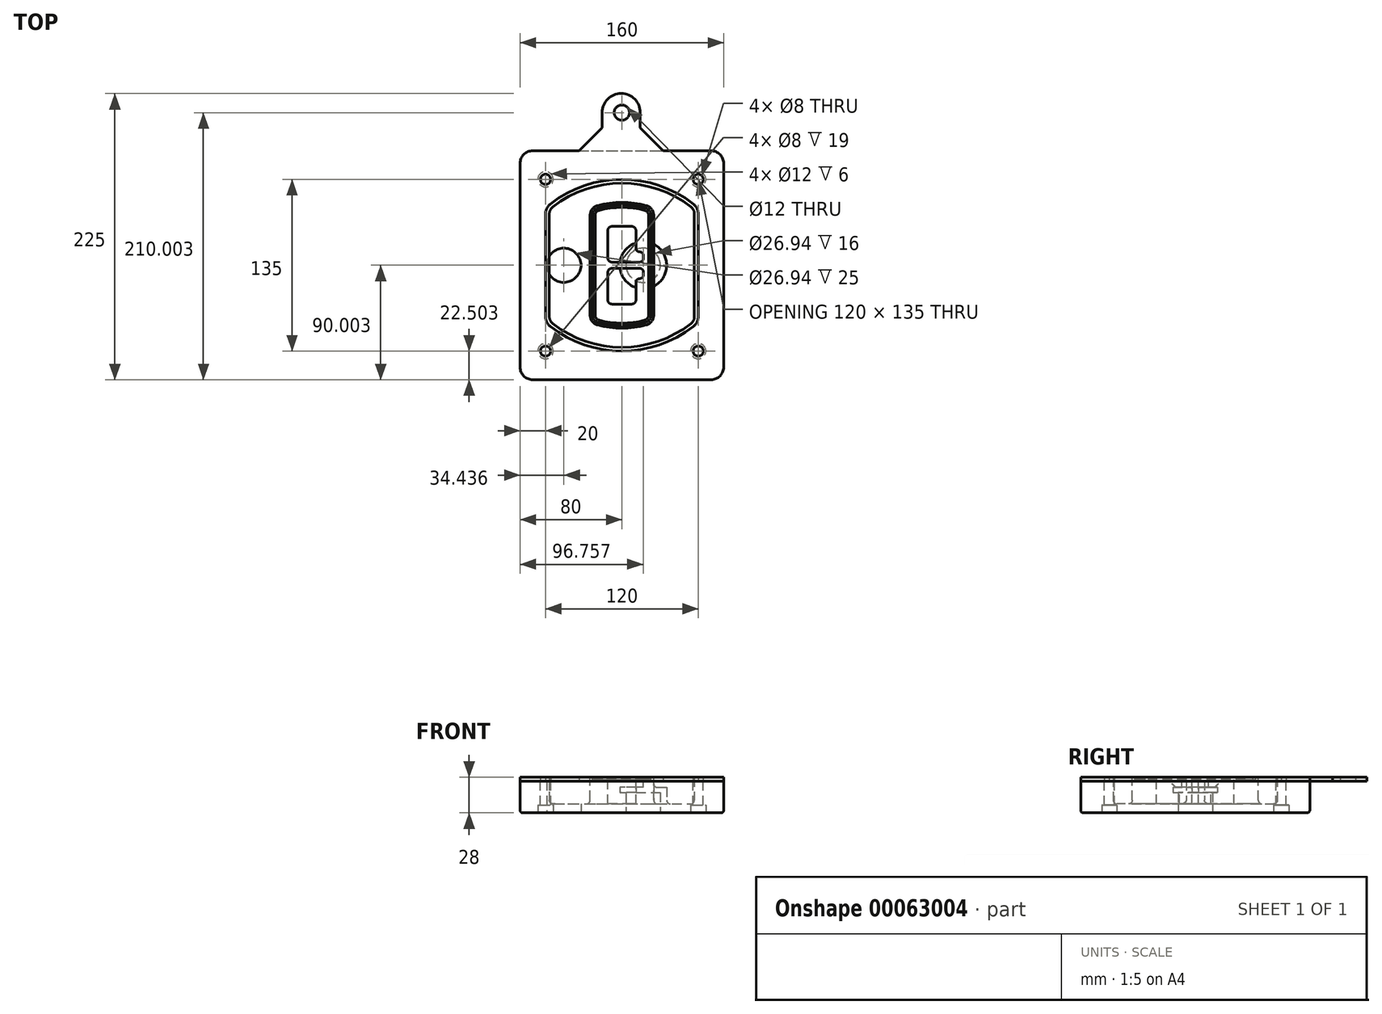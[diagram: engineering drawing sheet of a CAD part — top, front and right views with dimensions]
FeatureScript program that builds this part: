
annotation { "Feature Type Name" : "Feature", "Feature Type Description" : "" }
export const myFeature = defineFeature(function(context is Context, id is Id, definition is map)
    precondition{}
    {
        {
            var Q0;
            Q0=qCreatedBy(makeId("Top.planeOp"),FACE);
            var sketch = newSketch(context, id + "F0", { "sketchPlane" : qUnion([Q0])});
            skPoint(sketch, "E0.rect.middle", {"position": v(0, 0) * mm});
            skLineSegment(sketch, "E1.bottom", {"start": v(24.05, 28.38) * mm, "end": v(164.05, 28.38) * mm});
            skLineSegment(sketch, "E1.top", {"start": v(24.05, 208.38) * mm, "end": v(164.05, 208.38) * mm});
            skLineSegment(sketch, "E1.left", {"start": v(14.05, 38.38) * mm, "end": v(14.05, 198.38) * mm});
            skLineSegment(sketch, "E1.right", {"start": v(174.05, 38.38) * mm, "end": v(174.05, 198.38) * mm});
            skLineSegment(sketch, "E2", {"start": v(14.05, 208.38) * mm, "end": v(174.05, 28.38) * mm, "construction": true});
            skLineSegment(sketch, "E3", {"start": v(174.05, 208.38) * mm, "end": v(14.05, 28.38) * mm, "construction": true});
            skCircle(sketch, "E4", {"center": v(34.05, 185.88) * mm, "radius": 4 * mm});
            skCircle(sketch, "E5", {"center": v(154.05, 185.88) * mm, "radius": 4 * mm});
            skCircle(sketch, "E6", {"center": v(154.05, 50.88) * mm, "radius": 4 * mm});
            skCircle(sketch, "E7", {"center": v(34.05, 50.88) * mm, "radius": 4 * mm});
            skLineSegment(sketch, "E8", {"start": v(34.05, 185.88) * mm, "end": v(154.05, 185.88) * mm, "construction": true});
            skLineSegment(sketch, "E9", {"start": v(154.05, 185.88) * mm, "end": v(154.05, 50.88) * mm, "construction": true});
            skLineSegment(sketch, "E10", {"start": v(154.05, 50.88) * mm, "end": v(34.05, 50.88) * mm, "construction": true});
            skLineSegment(sketch, "E11", {"start": v(34.05, 50.88) * mm, "end": v(34.05, 185.88) * mm, "construction": true});
            skLineSegment(sketch, "E12", {"start": v(34.05, 158.68) * mm, "end": v(34.05, 78.09) * mm});
            skLineSegment(sketch, "E13", {"start": v(154.05, 158.68) * mm, "end": v(154.05, 78.09) * mm});
            skArc(sketch, "E14", {"start": v(150.2, 166.56) * mm, "mid": v(94.05, 185.88) * mm, "end": v(37.9, 166.56) * mm});
            skArc(sketch, "E15", {"start": v(37.9, 70.2) * mm, "mid": v(94.05, 50.88) * mm, "end": v(150.2, 70.2) * mm});
            skLineSegment(sketch, "E16", {"start": v(34.05, 118.38) * mm, "end": v(154.05, 118.38) * mm, "construction": true});
            skPoint(sketch, "E17.visualSharp", {"position": v(34.05, 73.38) * mm});
            skArc(sketch, "E17.filletArc", {"start": v(34.05, 78.09) * mm, "mid": v(35.06, 73.7) * mm, "end": v(37.9, 70.2) * mm});
            skPoint(sketch, "E18.visualSharp", {"position": v(34.05, 163.38) * mm});
            skArc(sketch, "E18.filletArc", {"start": v(37.9, 166.56) * mm, "mid": v(35.06, 163.06) * mm, "end": v(34.05, 158.68) * mm});
            skPoint(sketch, "E19.visualSharp", {"position": v(154.05, 163.38) * mm});
            skArc(sketch, "E19.filletArc", {"start": v(154.05, 158.68) * mm, "mid": v(153.04, 163.06) * mm, "end": v(150.2, 166.56) * mm});
            skPoint(sketch, "E20.visualSharp", {"position": v(154.05, 73.38) * mm});
            skArc(sketch, "E20.filletArc", {"start": v(150.2, 70.2) * mm, "mid": v(153.04, 73.7) * mm, "end": v(154.05, 78.09) * mm});
            skPoint(sketch, "E21.visualSharp", {"position": v(14.05, 208.38) * mm});
            skArc(sketch, "E21.filletArc", {"start": v(24.05, 208.38) * mm, "mid": v(16.98, 205.45) * mm, "end": v(14.05, 198.38) * mm});
            skPoint(sketch, "E22.visualSharp", {"position": v(174.05, 208.38) * mm});
            skArc(sketch, "E22.filletArc", {"start": v(174.05, 198.38) * mm, "mid": v(171.12, 205.45) * mm, "end": v(164.05, 208.38) * mm});
            skPoint(sketch, "E23.visualSharp", {"position": v(174.05, 28.38) * mm});
            skArc(sketch, "E23.filletArc", {"start": v(164.05, 28.38) * mm, "mid": v(171.12, 31.31) * mm, "end": v(174.05, 38.38) * mm});
            skPoint(sketch, "E24.visualSharp", {"position": v(14.05, 28.38) * mm});
            skArc(sketch, "E24.filletArc", {"start": v(14.05, 38.38) * mm, "mid": v(16.98, 31.31) * mm, "end": v(24.05, 28.38) * mm});
            skArc(sketch, "E25.0", {"start": v(151.05, 158.68) * mm, "mid": v(150.34, 161.75) * mm, "end": v(148.36, 164.2) * mm});
            skLineSegment(sketch, "E25.1", {"start": v(151.05, 158.68) * mm, "end": v(151.05, 78.09) * mm});
            skArc(sketch, "E25.2", {"start": v(148.36, 72.57) * mm, "mid": v(150.34, 75.02) * mm, "end": v(151.05, 78.09) * mm});
            skArc(sketch, "E25.3", {"start": v(39.74, 72.57) * mm, "mid": v(94.05, 53.88) * mm, "end": v(148.36, 72.57) * mm});
            skArc(sketch, "E25.4", {"start": v(37.05, 78.09) * mm, "mid": v(37.76, 75.02) * mm, "end": v(39.74, 72.57) * mm});
            skArc(sketch, "E25.5", {"start": v(148.36, 164.2) * mm, "mid": v(94.05, 182.88) * mm, "end": v(39.74, 164.2) * mm});
            skLineSegment(sketch, "E25.6", {"start": v(37.05, 158.68) * mm, "end": v(37.05, 78.09) * mm});
            skArc(sketch, "E25.7", {"start": v(39.74, 164.2) * mm, "mid": v(37.76, 161.75) * mm, "end": v(37.05, 158.68) * mm});
            skArc(sketch, "E26.0", {"start": v(35.43, 169.71) * mm, "mid": v(31.47, 164.82) * mm, "end": v(30.05, 158.68) * mm});
            skArc(sketch, "E26.1", {"start": v(152.67, 169.71) * mm, "mid": v(94.05, 189.88) * mm, "end": v(35.43, 169.71) * mm});
            skArc(sketch, "E26.2", {"start": v(158.05, 158.68) * mm, "mid": v(156.63, 164.82) * mm, "end": v(152.67, 169.71) * mm});
            skLineSegment(sketch, "E26.3", {"start": v(158.05, 158.68) * mm, "end": v(158.05, 78.09) * mm});
            skArc(sketch, "E26.4", {"start": v(152.67, 67.05) * mm, "mid": v(156.63, 71.95) * mm, "end": v(158.05, 78.09) * mm});
            skLineSegment(sketch, "E26.5", {"start": v(30.05, 158.68) * mm, "end": v(30.05, 78.09) * mm});
            skArc(sketch, "E26.6", {"start": v(35.43, 67.05) * mm, "mid": v(94.05, 46.88) * mm, "end": v(152.67, 67.05) * mm});
            skArc(sketch, "E26.7", {"start": v(30.05, 78.09) * mm, "mid": v(31.47, 71.95) * mm, "end": v(35.43, 67.05) * mm});
            skSolve(sketch);
        }
        {
            var Q0;
            Q0=makeQuery(id+"F0.imprint","IMPRINT",FACE,{"disambiguationData":[TD([[makeQuery(id+"F0.imprint","IMPRINT",EDGE,{"derivedFrom":sQuery(id+"F0.wireOp",EDGE,"E1.bottom")}),1.0]])]});
            var Q1;
            Q1=makeQuery(id+"F0.imprint","IMPRINT",FACE,{"disambiguationData":[TD([[makeQuery(id+"F0.imprint","IMPRINT",EDGE,{"derivedFrom":sQuery(id+"F0.wireOp",EDGE,"E12")}),1.0]])]});
            var Q2;
            Q2=makeQuery(id+"F0.imprint","IMPRINT",FACE,{"disambiguationData":[TD([[makeQuery(id+"F0.imprint","IMPRINT",EDGE,{"derivedFrom":sQuery(id+"F0.wireOp",EDGE,"E25.0")}),1.0]])]});
            var Q3;
            Q3=makeQuery(id+"F0.imprint","IMPRINT",FACE,{"disambiguationData":[TD([[makeQuery(id+"F0.imprint","IMPRINT",EDGE,{"derivedFrom":sQuery(id+"F0.wireOp",EDGE,"E12")}),-1.0]])]});
            extrude(context, id + "F1", {"entities" : qUnion([Q0, Q1, Q2, Q3]), "oppositeDirection" : true, "depth" : 25 * mm});
        }
        {
            var Q0;
            Q0=makeQuery(id+"F0.imprint","IMPRINT",FACE,{"disambiguationData":[TD([[makeQuery(id+"F0.imprint","IMPRINT",EDGE,{"derivedFrom":sQuery(id+"F0.wireOp",EDGE,"E12")}),1.0]])]});
            extrude(context, id + "F2", {"entities" : qUnion([Q0]), "operationType" : NewBodyOperationType.ADD, "depth" : 3 * mm});
        }
        {
            var Q0;
            Q0=makeQuery(id+"F0.imprint","IMPRINT",FACE,{"disambiguationData":[TD([[makeQuery(id+"F0.imprint","IMPRINT",EDGE,{"derivedFrom":sQuery(id+"F0.wireOp",EDGE,"E25.0")}),1.0]])]});
            extrude(context, id + "F3", {"entities" : qUnion([Q0]), "operationType" : NewBodyOperationType.REMOVE, "oppositeDirection" : true, "depth" : 18 * mm});
        }
        {
            var Q0;
            Q0=makeQuery(id+"F2.opExtrude","CAP_FACE",FACE,{"disambiguationData":[OSD([sQuery(id+"F0.wireOp",EDGE,"E12"),sQuery(id+"F0.wireOp",EDGE,"E13"),sQuery(id+"F0.wireOp",EDGE,"E14"),sQuery(id+"F0.wireOp",EDGE,"E15"),sQuery(id+"F0.wireOp",EDGE,"E17.filletArc"),sQuery(id+"F0.wireOp",EDGE,"E18.filletArc"),sQuery(id+"F0.wireOp",EDGE,"E19.filletArc"),sQuery(id+"F0.wireOp",EDGE,"E20.filletArc"),sQuery(id+"F0.wireOp",EDGE,"E25.0"),sQuery(id+"F0.wireOp",EDGE,"E25.1"),sQuery(id+"F0.wireOp",EDGE,"E25.2"),sQuery(id+"F0.wireOp",EDGE,"E25.3"),sQuery(id+"F0.wireOp",EDGE,"E25.4"),sQuery(id+"F0.wireOp",EDGE,"E25.5"),sQuery(id+"F0.wireOp",EDGE,"E25.6"),sQuery(id+"F0.wireOp",EDGE,"E25.7")])],"isStart":false});
            var sketch = newSketch(context, id + "F4", { "sketchPlane" : qUnion([Q0])});
            skArc(sketch, "E27.0", {"start": v(74.97, 71.41) * mm, "mid": v(94.05, 68.88) * mm, "end": v(113.13, 71.41) * mm});
            skArc(sketch, "E28.0", {"start": v(113.13, 165.35) * mm, "mid": v(94.05, 167.88) * mm, "end": v(74.97, 165.35) * mm});
            skLineSegment(sketch, "E29", {"start": v(69.05, 157.63) * mm, "end": v(69.05, 79.14) * mm});
            skLineSegment(sketch, "E30", {"start": v(119.05, 157.63) * mm, "end": v(119.05, 79.14) * mm});
            skLineSegment(sketch, "E31", {"start": v(69.05, 163.48) * mm, "end": v(119.05, 163.48) * mm, "construction": true});
            skLineSegment(sketch, "E32", {"start": v(69.05, 73.28) * mm, "end": v(119.05, 73.28) * mm, "construction": true});
            skPoint(sketch, "E33.visualSharp", {"position": v(69.05, 163.48) * mm});
            skArc(sketch, "E33.filletArc", {"start": v(74.97, 165.35) * mm, "mid": v(70.7, 162.5) * mm, "end": v(69.05, 157.63) * mm});
            skPoint(sketch, "E34.visualSharp", {"position": v(119.05, 163.48) * mm});
            skArc(sketch, "E34.filletArc", {"start": v(119.05, 157.63) * mm, "mid": v(117.4, 162.5) * mm, "end": v(113.13, 165.35) * mm});
            skPoint(sketch, "E35.visualSharp", {"position": v(119.05, 73.28) * mm});
            skArc(sketch, "E35.filletArc", {"start": v(113.13, 71.41) * mm, "mid": v(117.4, 74.27) * mm, "end": v(119.05, 79.14) * mm});
            skPoint(sketch, "E36.visualSharp", {"position": v(69.05, 73.28) * mm});
            skArc(sketch, "E36.filletArc", {"start": v(69.05, 79.14) * mm, "mid": v(70.7, 74.27) * mm, "end": v(74.97, 71.41) * mm});
            skArc(sketch, "E37.0", {"start": v(148.36, 164.2) * mm, "mid": v(94.05, 182.88) * mm, "end": v(39.74, 164.2) * mm});
            skArc(sketch, "E37.1", {"start": v(39.74, 164.2) * mm, "mid": v(37.76, 161.75) * mm, "end": v(37.05, 158.68) * mm});
            skLineSegment(sketch, "E37.2", {"start": v(37.05, 158.68) * mm, "end": v(37.05, 78.09) * mm});
            skArc(sketch, "E37.3", {"start": v(37.05, 78.09) * mm, "mid": v(37.76, 75.02) * mm, "end": v(39.74, 72.57) * mm});
            skArc(sketch, "E37.4", {"start": v(39.74, 72.57) * mm, "mid": v(94.05, 53.88) * mm, "end": v(148.36, 72.57) * mm});
            skArc(sketch, "E37.5", {"start": v(148.36, 72.57) * mm, "mid": v(150.34, 75.02) * mm, "end": v(151.05, 78.09) * mm});
            skLineSegment(sketch, "E37.6", {"start": v(151.05, 158.68) * mm, "end": v(151.05, 78.09) * mm});
            skArc(sketch, "E37.7", {"start": v(151.05, 158.68) * mm, "mid": v(150.34, 161.75) * mm, "end": v(148.36, 164.2) * mm});
            skLineSegment(sketch, "E38.0", {"start": v(117.05, 157.63) * mm, "end": v(117.05, 79.14) * mm});
            skArc(sketch, "E38.1", {"start": v(112.61, 73.34) * mm, "mid": v(115.81, 75.49) * mm, "end": v(117.05, 79.14) * mm});
            skArc(sketch, "E38.2", {"start": v(75.49, 73.34) * mm, "mid": v(94.05, 70.88) * mm, "end": v(112.61, 73.34) * mm});
            skArc(sketch, "E38.3", {"start": v(71.05, 79.14) * mm, "mid": v(72.29, 75.49) * mm, "end": v(75.49, 73.34) * mm});
            skLineSegment(sketch, "E38.4", {"start": v(71.05, 157.63) * mm, "end": v(71.05, 79.14) * mm});
            skArc(sketch, "E38.5", {"start": v(117.05, 157.63) * mm, "mid": v(115.81, 161.28) * mm, "end": v(112.61, 163.42) * mm});
            skArc(sketch, "E38.6", {"start": v(75.49, 163.42) * mm, "mid": v(72.29, 161.28) * mm, "end": v(71.05, 157.63) * mm});
            skArc(sketch, "E38.7", {"start": v(112.61, 163.42) * mm, "mid": v(94.05, 165.88) * mm, "end": v(75.49, 163.42) * mm});
            skArc(sketch, "E39.0", {"start": v(115.05, 157.63) * mm, "mid": v(114.23, 160.06) * mm, "end": v(112.1, 161.5) * mm});
            skLineSegment(sketch, "E39.1", {"start": v(115.05, 157.63) * mm, "end": v(115.05, 79.14) * mm});
            skArc(sketch, "E39.2", {"start": v(112.1, 75.27) * mm, "mid": v(114.23, 76.7) * mm, "end": v(115.05, 79.14) * mm});
            skArc(sketch, "E39.3", {"start": v(76, 75.27) * mm, "mid": v(94.05, 72.88) * mm, "end": v(112.1, 75.27) * mm});
            skArc(sketch, "E39.4", {"start": v(73.05, 79.14) * mm, "mid": v(73.87, 76.7) * mm, "end": v(76, 75.27) * mm});
            skArc(sketch, "E39.5", {"start": v(112.1, 161.5) * mm, "mid": v(94.05, 163.88) * mm, "end": v(76, 161.5) * mm});
            skLineSegment(sketch, "E39.6", {"start": v(73.05, 157.63) * mm, "end": v(73.05, 79.14) * mm});
            skArc(sketch, "E39.7", {"start": v(76, 161.5) * mm, "mid": v(73.87, 160.06) * mm, "end": v(73.05, 157.63) * mm});
            skLineSegment(sketch, "E40", {"start": v(69.05, 118.38) * mm, "end": v(119.05, 118.38) * mm, "construction": true});
            skLineSegment(sketch, "E41", {"start": v(83.05, 123.88) * mm, "end": v(83.05, 145.88) * mm});
            skLineSegment(sketch, "E42", {"start": v(86.05, 148.88) * mm, "end": v(102.05, 148.88) * mm});
            skLineSegment(sketch, "E43", {"start": v(105.05, 145.88) * mm, "end": v(105.05, 131.88) * mm});
            skLineSegment(sketch, "E44", {"start": v(108.05, 128.88) * mm, "end": v(108.05, 128.88) * mm});
            skLineSegment(sketch, "E45", {"start": v(111.05, 125.88) * mm, "end": v(111.05, 123.88) * mm});
            skLineSegment(sketch, "E46", {"start": v(108.05, 120.88) * mm, "end": v(86.05, 120.88) * mm});
            skPoint(sketch, "E47.visualSharp", {"position": v(83.05, 148.88) * mm});
            skArc(sketch, "E47.filletArc", {"start": v(86.05, 148.88) * mm, "mid": v(83.93, 148) * mm, "end": v(83.05, 145.88) * mm});
            skPoint(sketch, "E48.visualSharp", {"position": v(105.05, 148.88) * mm});
            skArc(sketch, "E48.filletArc", {"start": v(105.05, 145.88) * mm, "mid": v(104.17, 148) * mm, "end": v(102.05, 148.88) * mm});
            skPoint(sketch, "E49.visualSharp", {"position": v(105.05, 128.88) * mm});
            skArc(sketch, "E49.filletArc", {"start": v(105.05, 131.88) * mm, "mid": v(105.93, 129.76) * mm, "end": v(108.05, 128.88) * mm});
            skPoint(sketch, "E50.visualSharp", {"position": v(111.05, 128.88) * mm});
            skArc(sketch, "E50.filletArc", {"start": v(111.05, 125.88) * mm, "mid": v(110.17, 128) * mm, "end": v(108.05, 128.88) * mm});
            skPoint(sketch, "E51.visualSharp", {"position": v(111.05, 120.88) * mm});
            skArc(sketch, "E51.filletArc", {"start": v(108.05, 120.88) * mm, "mid": v(110.17, 121.76) * mm, "end": v(111.05, 123.88) * mm});
            skPoint(sketch, "E52.visualSharp", {"position": v(83.05, 120.88) * mm});
            skArc(sketch, "E52.filletArc", {"start": v(83.05, 123.88) * mm, "mid": v(83.93, 121.76) * mm, "end": v(86.05, 120.88) * mm});
            skLineSegment(sketch, "E53.0.MirrorCS", {"start": v(108.05, 115.88) * mm, "end": v(86.05, 115.88) * mm});
            skArc(sketch, "E54.0.MirrorCS", {"start": v(83.05, 112.88) * mm, "mid": v(83.93, 115) * mm, "end": v(86.05, 115.88) * mm});
            skLineSegment(sketch, "E55.0.MirrorCS", {"start": v(83.05, 112.88) * mm, "end": v(83.05, 90.88) * mm});
            skArc(sketch, "E56.0.MirrorCS", {"start": v(86.05, 87.88) * mm, "mid": v(83.93, 88.76) * mm, "end": v(83.05, 90.88) * mm});
            skLineSegment(sketch, "E57.0.MirrorCS", {"start": v(86.05, 87.88) * mm, "end": v(102.05, 87.88) * mm});
            skArc(sketch, "E58.0.MirrorCS", {"start": v(105.05, 90.88) * mm, "mid": v(104.17, 88.76) * mm, "end": v(102.05, 87.88) * mm});
            skLineSegment(sketch, "E59.0.MirrorCS", {"start": v(105.05, 90.88) * mm, "end": v(105.05, 104.88) * mm});
            skArc(sketch, "E60.0.MirrorCS", {"start": v(105.05, 104.88) * mm, "mid": v(105.93, 107) * mm, "end": v(108.05, 107.88) * mm});
            skArc(sketch, "E61.0.MirrorCS", {"start": v(111.05, 110.88) * mm, "mid": v(110.17, 108.76) * mm, "end": v(108.05, 107.88) * mm});
            skLineSegment(sketch, "E62.0.MirrorCS", {"start": v(111.05, 110.88) * mm, "end": v(111.05, 112.88) * mm});
            skArc(sketch, "E63.0.MirrorCS", {"start": v(108.05, 115.88) * mm, "mid": v(110.17, 115) * mm, "end": v(111.05, 112.88) * mm});
            skSolve(sketch);
        }
        {
            var Q0;
            Q0=makeQuery(id+"F4.imprint","IMPRINT",FACE,{"disambiguationData":[TD([[makeQuery(id+"F4.imprint","IMPRINT",EDGE,{"derivedFrom":sQuery(id+"F4.wireOp",EDGE,"E27.0")}),1.0]])]});
            var Q1;
            Q1=makeQuery(id+"F4.imprint","IMPRINT",FACE,{"disambiguationData":[TD([[makeQuery(id+"F4.imprint","IMPRINT",EDGE,{"derivedFrom":sQuery(id+"F4.wireOp",EDGE,"E38.0")}),-1.0]])]});
            var Q2;
            Q2=makeQuery(id+"F4.imprint","IMPRINT",FACE,{"disambiguationData":[TD([[makeQuery(id+"F4.imprint","IMPRINT",EDGE,{"derivedFrom":sQuery(id+"F4.wireOp",EDGE,"E39.0")}),1.0]])]});
            extrude(context, id + "F5", {"entities" : qUnion([Q0, Q1, Q2]), "operationType" : NewBodyOperationType.ADD, "endBound" : BoundingType.UP_TO_NEXT, "oppositeDirection" : true, "depth" : 25 * mm});
        }
        {
            var Q0;
            Q0=makeQuery(id+"F4.imprint","IMPRINT",FACE,{"disambiguationData":[TD([[makeQuery(id+"F4.imprint","IMPRINT",EDGE,{"derivedFrom":sQuery(id+"F4.wireOp",EDGE,"E38.0")}),-1.0]])]});
            extrude(context, id + "F6", {"entities" : qUnion([Q0]), "operationType" : NewBodyOperationType.REMOVE, "oppositeDirection" : true, "depth" : 2 * mm});
        }
        {
            var Q0;
            Q0=makeQuery(id+"F1.opExtrude","CAP_FACE",FACE,{"disambiguationData":[OSD([sQuery(id+"F0.wireOp",EDGE,"E1.bottom"),sQuery(id+"F0.wireOp",EDGE,"E1.top"),sQuery(id+"F0.wireOp",EDGE,"E1.left"),sQuery(id+"F0.wireOp",EDGE,"E1.right"),sQuery(id+"F0.wireOp",EDGE,"E4"),sQuery(id+"F0.wireOp",EDGE,"E5"),sQuery(id+"F0.wireOp",EDGE,"E6"),sQuery(id+"F0.wireOp",EDGE,"E7"),sQuery(id+"F0.wireOp",EDGE,"E21.filletArc"),sQuery(id+"F0.wireOp",EDGE,"E22.filletArc"),sQuery(id+"F0.wireOp",EDGE,"E23.filletArc"),sQuery(id+"F0.wireOp",EDGE,"E24.filletArc")])],"isStart":false});
            var sketch = newSketch(context, id + "F7", { "sketchPlane" : qUnion([Q0])});
            skCircle(sketch, "E64", {"center": v(110.8, -118.38) * mm, "radius": 13.47 * mm});
            skCircle(sketch, "E65", {"center": v(48.49, -118.38) * mm, "radius": 13.47 * mm});
            skLineSegment(sketch, "E66", {"start": v(174.05, -118.38) * mm, "end": v(14.05, -118.38) * mm});
            skCircle(sketch, "E67", {"center": v(110.8, -118.38) * mm, "radius": 18.47 * mm});
            skCircle(sketch, "E68", {"center": v(154.05, -185.88) * mm, "radius": 6 * mm});
            skCircle(sketch, "E69", {"center": v(34.05, -185.88) * mm, "radius": 6 * mm});
            skCircle(sketch, "E70", {"center": v(34.05, -50.88) * mm, "radius": 6 * mm});
            skCircle(sketch, "E71", {"center": v(154.05, -50.88) * mm, "radius": 6 * mm});
            skSolve(sketch);
        }
        {
            var Q0;
            {var subQ1=sQuery(id+"F7.wireOp",EDGE,"E66");var subQ4=sQuery(id+"F7.wireOp",EDGE,"E64");var subQ6=makeQuery(id+"F7.imprint","INTERSECT",VERTEX,{"disambiguationData":[OD(0.0)],"derivedFrom":[subQ4,subQ1]});Q0=makeQuery(id+"F7.imprint","IMPRINT",FACE,{"disambiguationData":[TD([[makeQuery(id+"F7.imprint","IMPRINT",EDGE,{"disambiguationData":[TD([[subQ6,-1.0]])],"derivedFrom":subQ4}),-1.0]])]});}
            var Q1;
            {var subQ0=sQuery(id+"F7.wireOp",EDGE,"E66");var subQ1=sQuery(id+"F7.wireOp",EDGE,"E64");var subQ3=makeQuery(id+"F7.imprint","INTERSECT",VERTEX,{"disambiguationData":[OD(0.0)],"derivedFrom":[subQ1,subQ0]});Q1=makeQuery(id+"F7.imprint","IMPRINT",FACE,{"disambiguationData":[TD([[makeQuery(id+"F7.imprint","IMPRINT",EDGE,{"disambiguationData":[TD([[subQ3,-1.0]])],"derivedFrom":subQ1}),1.0]])]});}
            var Q2;
            {var subQ0=sQuery(id+"F7.wireOp",EDGE,"E66");var subQ1=sQuery(id+"F7.wireOp",EDGE,"E64");var subQ3=makeQuery(id+"F7.imprint","INTERSECT",VERTEX,{"disambiguationData":[OD(0.0)],"derivedFrom":[subQ1,subQ0]});Q2=makeQuery(id+"F7.imprint","IMPRINT",FACE,{"disambiguationData":[TD([[makeQuery(id+"F7.imprint","IMPRINT",EDGE,{"disambiguationData":[TD([[subQ3,1.0]])],"derivedFrom":subQ1}),1.0]])]});}
            var Q3;
            {var subQ1=sQuery(id+"F7.wireOp",EDGE,"E66");var subQ4=sQuery(id+"F7.wireOp",EDGE,"E64");var subQ6=makeQuery(id+"F7.imprint","INTERSECT",VERTEX,{"disambiguationData":[OD(0.0)],"derivedFrom":[subQ4,subQ1]});Q3=makeQuery(id+"F7.imprint","IMPRINT",FACE,{"disambiguationData":[TD([[makeQuery(id+"F7.imprint","IMPRINT",EDGE,{"disambiguationData":[TD([[subQ6,1.0]])],"derivedFrom":subQ4}),-1.0]])]});}
            extrude(context, id + "F8", {"entities" : qUnion([Q0, Q1, Q2, Q3]), "operationType" : NewBodyOperationType.ADD, "oppositeDirection" : true, "depth" : 20 * mm});
        }
        {
            var Q0;
            {var subQ0=sQuery(id+"F7.wireOp",EDGE,"E66");var subQ1=sQuery(id+"F7.wireOp",EDGE,"E64");var subQ3=makeQuery(id+"F7.imprint","INTERSECT",VERTEX,{"disambiguationData":[OD(0.0)],"derivedFrom":[subQ1,subQ0]});Q0=makeQuery(id+"F7.imprint","IMPRINT",FACE,{"disambiguationData":[TD([[makeQuery(id+"F7.imprint","IMPRINT",EDGE,{"disambiguationData":[TD([[subQ3,-1.0]])],"derivedFrom":subQ1}),1.0]])]});}
            var Q1;
            {var subQ0=sQuery(id+"F7.wireOp",EDGE,"E66");var subQ1=sQuery(id+"F7.wireOp",EDGE,"E64");var subQ3=makeQuery(id+"F7.imprint","INTERSECT",VERTEX,{"disambiguationData":[OD(0.0)],"derivedFrom":[subQ1,subQ0]});Q1=makeQuery(id+"F7.imprint","IMPRINT",FACE,{"disambiguationData":[TD([[makeQuery(id+"F7.imprint","IMPRINT",EDGE,{"disambiguationData":[TD([[subQ3,1.0]])],"derivedFrom":subQ1}),1.0]])]});}
            extrude(context, id + "F9", {"entities" : qUnion([Q0, Q1]), "operationType" : NewBodyOperationType.REMOVE, "oppositeDirection" : true, "depth" : 16 * mm});
        }
        {
            var Q0;
            {var subQ0=sQuery(id+"F7.wireOp",EDGE,"E66");var subQ1=sQuery(id+"F7.wireOp",EDGE,"E65");var subQ3=makeQuery(id+"F7.imprint","INTERSECT",VERTEX,{"disambiguationData":[OD(0.0)],"derivedFrom":[subQ1,subQ0]});Q0=makeQuery(id+"F7.imprint","IMPRINT",FACE,{"disambiguationData":[TD([[makeQuery(id+"F7.imprint","IMPRINT",EDGE,{"disambiguationData":[TD([[subQ3,-1.0]])],"derivedFrom":subQ1}),1.0]])]});}
            var Q1;
            {var subQ0=sQuery(id+"F7.wireOp",EDGE,"E66");var subQ1=sQuery(id+"F7.wireOp",EDGE,"E65");var subQ3=makeQuery(id+"F7.imprint","INTERSECT",VERTEX,{"disambiguationData":[OD(0.0)],"derivedFrom":[subQ1,subQ0]});Q1=makeQuery(id+"F7.imprint","IMPRINT",FACE,{"disambiguationData":[TD([[makeQuery(id+"F7.imprint","IMPRINT",EDGE,{"disambiguationData":[TD([[subQ3,1.0]])],"derivedFrom":subQ1}),1.0]])]});}
            extrude(context, id + "F10", {"entities" : qUnion([Q0, Q1]), "operationType" : NewBodyOperationType.REMOVE, "oppositeDirection" : true, "depth" : 25 * mm});
        }
        {
            var Q0;
            Q0=makeQuery(id+"F7.imprint","IMPRINT",FACE,{"disambiguationData":[TD([[makeQuery(id+"F7.imprint","IMPRINT",EDGE,{"derivedFrom":sQuery(id+"F7.wireOp",EDGE,"E68")}),1.0]])]});
            var Q1;
            Q1=makeQuery(id+"F7.imprint","IMPRINT",FACE,{"disambiguationData":[TD([[makeQuery(id+"F7.imprint","IMPRINT",EDGE,{"derivedFrom":makeQuery(id+"F1.opExtrude","CAP_EDGE",EDGE,{"disambiguationData":[OSD([sQuery(id+"F0.wireOp",EDGE,"E5")])],"isStart":false})}),-1.0]])]});
            var Q2;
            Q2=makeQuery(id+"F7.imprint","IMPRINT",FACE,{"disambiguationData":[TD([[makeQuery(id+"F7.imprint","IMPRINT",EDGE,{"derivedFrom":sQuery(id+"F7.wireOp",EDGE,"E69")}),1.0]])]});
            var Q3;
            Q3=makeQuery(id+"F7.imprint","IMPRINT",FACE,{"disambiguationData":[TD([[makeQuery(id+"F7.imprint","IMPRINT",EDGE,{"derivedFrom":makeQuery(id+"F1.opExtrude","CAP_EDGE",EDGE,{"disambiguationData":[OSD([sQuery(id+"F0.wireOp",EDGE,"E4")])],"isStart":false})}),-1.0]])]});
            var Q4;
            Q4=makeQuery(id+"F7.imprint","IMPRINT",FACE,{"disambiguationData":[TD([[makeQuery(id+"F7.imprint","IMPRINT",EDGE,{"derivedFrom":sQuery(id+"F7.wireOp",EDGE,"E70")}),1.0]])]});
            var Q5;
            Q5=makeQuery(id+"F7.imprint","IMPRINT",FACE,{"disambiguationData":[TD([[makeQuery(id+"F7.imprint","IMPRINT",EDGE,{"derivedFrom":makeQuery(id+"F1.opExtrude","CAP_EDGE",EDGE,{"disambiguationData":[OSD([sQuery(id+"F0.wireOp",EDGE,"E7")])],"isStart":false})}),-1.0]])]});
            var Q6;
            Q6=makeQuery(id+"F7.imprint","IMPRINT",FACE,{"disambiguationData":[TD([[makeQuery(id+"F7.imprint","IMPRINT",EDGE,{"derivedFrom":sQuery(id+"F7.wireOp",EDGE,"E71")}),1.0]])]});
            var Q7;
            Q7=makeQuery(id+"F7.imprint","IMPRINT",FACE,{"disambiguationData":[TD([[makeQuery(id+"F7.imprint","IMPRINT",EDGE,{"derivedFrom":makeQuery(id+"F1.opExtrude","CAP_EDGE",EDGE,{"disambiguationData":[OSD([sQuery(id+"F0.wireOp",EDGE,"E6")])],"isStart":false})}),-1.0]])]});
            extrude(context, id + "F11", {"entities" : qUnion([Q0, Q1, Q2, Q3, Q4, Q5, Q6, Q7]), "operationType" : NewBodyOperationType.REMOVE, "oppositeDirection" : true, "depth" : 6 * mm});
        }
        {
            var Q0;
            Q0=makeQuery(id+"F9.boolean.opBoolean","COPY",FACE,{"derivedFrom":makeQuery(id+"F9.opExtrude","CAP_FACE",FACE,{"disambiguationData":[OSD([sQuery(id+"F7.wireOp",EDGE,"E64")])],"isStart":false})});
            var sketch = newSketch(context, id + "F12", { "sketchPlane" : qUnion([Q0])});
            skArc(sketch, "E72.0", {"start": v(105.05, -100.83) * mm, "mid": v(96.62, -106.56) * mm, "end": v(92.5, -115.88) * mm});
            skArc(sketch, "E72.1", {"start": v(92.5, -120.88) * mm, "mid": v(96.62, -130.2) * mm, "end": v(105.05, -135.93) * mm});
            skLineSegment(sketch, "E73", {"start": v(92.5, -120.88) * mm, "end": v(108.05, -120.88) * mm});
            skLineSegment(sketch, "E74.0", {"start": v(108.05, -115.88) * mm, "end": v(92.5, -115.88) * mm});
            skArc(sketch, "E74.1", {"start": v(108.05, -115.88) * mm, "mid": v(110.17, -115) * mm, "end": v(111.05, -112.88) * mm});
            skLineSegment(sketch, "E74.2", {"start": v(111.05, -110.88) * mm, "end": v(111.05, -112.88) * mm});
            skArc(sketch, "E74.3", {"start": v(111.05, -110.88) * mm, "mid": v(110.17, -108.76) * mm, "end": v(108.05, -107.88) * mm});
            skArc(sketch, "E74.4", {"start": v(105.05, -104.88) * mm, "mid": v(105.93, -107) * mm, "end": v(108.05, -107.88) * mm});
            skLineSegment(sketch, "E74.5", {"start": v(105.05, -100.83) * mm, "end": v(105.05, -104.88) * mm});
            skLineSegment(sketch, "E74.7", {"start": v(108.05, -120.88) * mm, "end": v(92.5, -120.88) * mm});
            skArc(sketch, "E74.8", {"start": v(108.05, -120.88) * mm, "mid": v(110.17, -121.76) * mm, "end": v(111.05, -123.88) * mm});
            skLineSegment(sketch, "E74.9", {"start": v(111.05, -125.88) * mm, "end": v(111.05, -123.88) * mm});
            skArc(sketch, "E74.10", {"start": v(111.05, -125.88) * mm, "mid": v(110.17, -128) * mm, "end": v(108.05, -128.88) * mm});
            skArc(sketch, "E74.11", {"start": v(105.05, -131.88) * mm, "mid": v(105.93, -129.76) * mm, "end": v(108.05, -128.88) * mm});
            skLineSegment(sketch, "E74.12", {"start": v(105.05, -135.93) * mm, "end": v(105.05, -131.88) * mm});
            skPoint(sketch, "E75.orphan", {"position": v(105.05, -145.88) * mm});
            skPoint(sketch, "E76.orphan", {"position": v(86.05, -120.88) * mm});
            skPoint(sketch, "E77.orphan", {"position": v(86.05, -115.88) * mm});
            skPoint(sketch, "E78.orphan", {"position": v(105.05, -90.88) * mm});
            skSolve(sketch);
        }
        {
            var Q0;
            {var subQ7=sQuery(id+"F12.wireOp",EDGE,"E72.0");var subQ14=sQuery(id+"F12.wireOp",EDGE,"E72.1");var subQ16=sQuery(id+"F12.wireOp",EDGE,"E74.1");var subQ18=sQuery(id+"F12.wireOp",EDGE,"E74.8");Q0=qUnion([makeQuery(id+"F12.imprint","IMPRINT",FACE,{"disambiguationData":[TD([[makeQuery(id+"F12.imprint","IMPRINT",EDGE,{"derivedFrom":subQ7}),1.0]])]}),makeQuery(id+"F12.imprint","IMPRINT",FACE,{"disambiguationData":[TD([[makeQuery(id+"F12.imprint","IMPRINT",EDGE,{"derivedFrom":subQ14}),1.0]])]}),makeQuery(id+"F12.imprint","IMPRINT",FACE,{"disambiguationData":[TD([[makeQuery(id+"F12.imprint","IMPRINT",EDGE,{"derivedFrom":subQ16}),1.0]])]}),makeQuery(id+"F12.imprint","IMPRINT",FACE,{"disambiguationData":[TD([[makeQuery(id+"F12.imprint","IMPRINT",EDGE,{"derivedFrom":subQ18}),-1.0]])]})]);}
            var Q1;
            Q1=makeQuery(id+"F5.boolean.opBoolean","SPLIT",FACE,{"disambiguationData":[TD([makeQuery(id+"F5.opExtrude","SWEPT_FACE",FACE,{"disambiguationData":[OSD([sQuery(id+"F4.wireOp",EDGE,"E41")])]})])],"derivedFrom":makeQuery(id+"F3.boolean.opBoolean","COPY",FACE,{"derivedFrom":makeQuery(id+"F3.opExtrude","CAP_FACE",FACE,{"disambiguationData":[OSD([sQuery(id+"F0.wireOp",EDGE,"E25.0"),sQuery(id+"F0.wireOp",EDGE,"E25.1"),sQuery(id+"F0.wireOp",EDGE,"E25.2"),sQuery(id+"F0.wireOp",EDGE,"E25.3"),sQuery(id+"F0.wireOp",EDGE,"E25.4"),sQuery(id+"F0.wireOp",EDGE,"E25.5"),sQuery(id+"F0.wireOp",EDGE,"E25.6"),sQuery(id+"F0.wireOp",EDGE,"E25.7")])],"isStart":false})})});
            extrude(context, id + "F13", {"entities" : qUnion([Q0]), "operationType" : NewBodyOperationType.REMOVE, "endBound" : BoundingType.UP_TO_SURFACE, "endBoundEntityFace" : qUnion([Q1]), "depth" : 25 * mm});
        }
        {
            var Q0;
            Q0=makeQuery(id+"F3.boolean.opBoolean","COPY",EDGE,{"derivedFrom":makeQuery(id+"F3.opExtrude","CAP_EDGE",EDGE,{"disambiguationData":[OSD([sQuery(id+"F0.wireOp",EDGE,"E25.6")])],"isStart":false})});
            var Q1;
            Q1=makeQuery(id+"F8.boolean.opBoolean","INTERSECT",EDGE,{"derivedFrom":[makeQuery(id+"F5.opExtrude","SWEPT_FACE",FACE,{"disambiguationData":[OSD([sQuery(id+"F4.wireOp",EDGE,"E30")])]}),makeQuery(id+"F8.opExtrude","CAP_FACE",FACE,{"disambiguationData":[OSD([sQuery(id+"F7.wireOp",EDGE,"E67")])],"isStart":false})]});
            var Q2;
            Q2=makeQuery(id+"F8.boolean.opBoolean","INTERSECT",EDGE,{"disambiguationData":[OD(1.0)],"derivedFrom":[makeQuery(id+"F5.opExtrude","SWEPT_FACE",FACE,{"disambiguationData":[OSD([sQuery(id+"F4.wireOp",EDGE,"E30")])]}),makeQuery(id+"F8.opExtrude","SWEPT_FACE",FACE,{"disambiguationData":[OSD([sQuery(id+"F7.wireOp",EDGE,"E67")])]})]});
            var Q3;
            {var subQ0=sQuery(id+"F4.wireOp",EDGE,"E30");Q3=makeQuery(id+"F8.boolean.opBoolean","SPLIT",EDGE,{"disambiguationData":[TD([makeQuery(id+"F5.opExtrude","SWEPT_FACE",FACE,{"disambiguationData":[OSD([sQuery(id+"F4.wireOp",EDGE,"E35.filletArc")])]})])],"derivedFrom":makeQuery(id+"F5.opExtrude","CAP_EDGE",EDGE,{"disambiguationData":[OSD([subQ0])],"isStart":false})});}
            var Q4;
            {var subQ0=sQuery(id+"F0.wireOp",EDGE,"E25.7");var subQ1=sQuery(id+"F0.wireOp",EDGE,"E25.1");var subQ2=sQuery(id+"F0.wireOp",EDGE,"E25.6");var subQ3=sQuery(id+"F0.wireOp",EDGE,"E25.5");var subQ4=sQuery(id+"F0.wireOp",EDGE,"E25.4");var subQ5=sQuery(id+"F0.wireOp",EDGE,"E25.0");var subQ6=sQuery(id+"F0.wireOp",EDGE,"E25.2");var subQ7=sQuery(id+"F0.wireOp",EDGE,"E25.3");Q4=makeQuery(id+"F8.boolean.opBoolean","INTERSECT",EDGE,{"derivedFrom":[makeQuery(id+"F5.boolean.opBoolean","SPLIT",FACE,{"disambiguationData":[TD([makeQuery(id+"F2.opExtrude","SWEPT_FACE",FACE,{"disambiguationData":[OSD([subQ5])]})])],"derivedFrom":makeQuery(id+"F3.boolean.opBoolean","COPY",FACE,{"derivedFrom":makeQuery(id+"F3.opExtrude","CAP_FACE",FACE,{"disambiguationData":[OSD([subQ5,subQ1,subQ6,subQ7,subQ4,subQ3,subQ2,subQ0])],"isStart":false})})}),makeQuery(id+"F8.opExtrude","SWEPT_FACE",FACE,{"disambiguationData":[OSD([sQuery(id+"F7.wireOp",EDGE,"E67")])]})]});}
            var Q5;
            Q5=makeQuery(id+"F8.boolean.opBoolean","INTERSECT",EDGE,{"disambiguationData":[OD(0.0)],"derivedFrom":[makeQuery(id+"F5.opExtrude","SWEPT_FACE",FACE,{"disambiguationData":[OSD([sQuery(id+"F4.wireOp",EDGE,"E30")])]}),makeQuery(id+"F8.opExtrude","SWEPT_FACE",FACE,{"disambiguationData":[OSD([sQuery(id+"F7.wireOp",EDGE,"E67")])]})]});
            fillet(context, id + "F14", {"entities" : qUnion([Q0, Q1, Q2, Q3, Q4, Q5]), "radius" : 3 * mm, "tangentPropagation" : true, "allowEdgeOverflow" : false});
        }
        {
            var Q0;
            Q0=makeQuery(id+"F1.opExtrude","CAP_EDGE",EDGE,{"disambiguationData":[OSD([sQuery(id+"F0.wireOp",EDGE,"E1.bottom")])],"isStart":false});
            fillet(context, id + "F15", {"entities" : qUnion([Q0]), "radius" : 2 * mm, "tangentPropagation" : true, "allowEdgeOverflow" : false});
        }
        {
            var Q0;
            {var subQ0=sQuery(id+"F0.wireOp",EDGE,"E22.filletArc");var subQ1=sQuery(id+"F0.wireOp",EDGE,"E7");var subQ2=sQuery(id+"F0.wireOp",EDGE,"E6");var subQ3=sQuery(id+"F0.wireOp",EDGE,"E5");var subQ4=sQuery(id+"F0.wireOp",EDGE,"E4");var subQ5=sQuery(id+"F0.wireOp",EDGE,"E1.bottom");var subQ6=sQuery(id+"F0.wireOp",EDGE,"E21.filletArc");var subQ7=sQuery(id+"F0.wireOp",EDGE,"E1.top");var subQ8=sQuery(id+"F0.wireOp",EDGE,"E1.left");var subQ9=sQuery(id+"F0.wireOp",EDGE,"E1.right");var subQ10=sQuery(id+"F0.wireOp",EDGE,"E23.filletArc");var subQ11=sQuery(id+"F0.wireOp",EDGE,"E24.filletArc");Q0=makeQuery(id+"F2.boolean.opBoolean","SPLIT",FACE,{"disambiguationData":[TD([makeQuery(id+"F1.opExtrude","SWEPT_FACE",FACE,{"disambiguationData":[OSD([subQ5])]})])],"derivedFrom":makeQuery(id+"F1.opExtrude","CAP_FACE",FACE,{"disambiguationData":[OSD([subQ5,subQ7,subQ8,subQ9,subQ4,subQ3,subQ2,subQ1,subQ6,subQ0,subQ10,subQ11])],"isStart":true})});}
            var sketch = newSketch(context, id + "F16", { "sketchPlane" : qUnion([Q0])});
            skLineSegment(sketch, "E79", {"start": v(94.05, 208.38) * mm, "end": v(94.05, 238.38) * mm, "construction": true});
            skCircle(sketch, "E80", {"center": v(94.05, 238.38) * mm, "radius": 6 * mm});
            skLineSegment(sketch, "E81", {"start": v(60.5, 208.38) * mm, "end": v(78.5, 226.38) * mm});
            skLineSegment(sketch, "E82", {"start": v(78.5, 226.38) * mm, "end": v(78.5, 238.38) * mm});
            skLineSegment(sketch, "E83", {"start": v(108.5, 238.38) * mm, "end": v(108.5, 226.38) * mm});
            skLineSegment(sketch, "E84", {"start": v(108.5, 226.38) * mm, "end": v(126.5, 208.38) * mm});
            skArc(sketch, "E85", {"start": v(108.5, 238.38) * mm, "mid": v(93.5, 253.38) * mm, "end": v(78.5, 238.38) * mm});
            skLineSegment(sketch, "E86", {"start": v(14.05, 118.38) * mm, "end": v(174.05, 118.38) * mm, "construction": true});
            skArc(sketch, "E87.MirrorCS", {"start": v(108.5, -1.62) * mm, "mid": v(93.5, -16.62) * mm, "end": v(78.5, -1.62) * mm});
            skCircle(sketch, "E88.MirrorC", {"center": v(94.05, -1.62) * mm, "radius": 6 * mm});
            skLineSegment(sketch, "E89.MirrorCS", {"start": v(78.5, 10.38) * mm, "end": v(78.5, -1.62) * mm});
            skLineSegment(sketch, "E90.MirrorCS", {"start": v(108.5, -1.62) * mm, "end": v(108.5, 10.38) * mm});
            skLineSegment(sketch, "E91.MirrorCS", {"start": v(108.5, 10.38) * mm, "end": v(126.5, 28.38) * mm});
            skLineSegment(sketch, "E92.MirrorCS", {"start": v(60.5, 28.38) * mm, "end": v(78.5, 10.38) * mm});
            skLineSegment(sketch, "E93.MirrorCS", {"start": v(94.05, 28.38) * mm, "end": v(94.05, -1.62) * mm, "construction": true});
            skSolve(sketch);
        }
        {
            var Q0;
            Q0=makeQuery(id+"F16.imprint","IMPRINT",FACE,{"disambiguationData":[TD([[makeQuery(id+"F16.imprint","IMPRINT",EDGE,{"derivedFrom":sQuery(id+"F16.wireOp",EDGE,"E80")}),-1.0]])]});
            var Q1;
            Q1=makeQuery(id+"F16.imprint","IMPRINT",FACE,{"disambiguationData":[TD([[makeQuery(id+"F16.imprint","IMPRINT",EDGE,{"derivedFrom":makeQuery(id+"F1.opExtrude","CAP_EDGE",EDGE,{"disambiguationData":[OSD([sQuery(id+"F0.wireOp",EDGE,"E1.left")])],"isStart":true})}),-1.0]])]});
            var Q2;
            Q2=makeQuery(id+"F16.imprint","IMPRINT",FACE,{"disambiguationData":[TD([[makeQuery(id+"F16.imprint","IMPRINT",EDGE,{"derivedFrom":sQuery(id+"F16.wireOp",EDGE,"E87.MirrorCS")}),-1.0]])]});
            var Q3;
            Q3=makeQuery(id+"F2.opExtrude","CAP_FACE",FACE,{"disambiguationData":[OSD([sQuery(id+"F0.wireOp",EDGE,"E12"),sQuery(id+"F0.wireOp",EDGE,"E13"),sQuery(id+"F0.wireOp",EDGE,"E14"),sQuery(id+"F0.wireOp",EDGE,"E15"),sQuery(id+"F0.wireOp",EDGE,"E17.filletArc"),sQuery(id+"F0.wireOp",EDGE,"E18.filletArc"),sQuery(id+"F0.wireOp",EDGE,"E19.filletArc"),sQuery(id+"F0.wireOp",EDGE,"E20.filletArc"),sQuery(id+"F0.wireOp",EDGE,"E25.0"),sQuery(id+"F0.wireOp",EDGE,"E25.1"),sQuery(id+"F0.wireOp",EDGE,"E25.2"),sQuery(id+"F0.wireOp",EDGE,"E25.3"),sQuery(id+"F0.wireOp",EDGE,"E25.4"),sQuery(id+"F0.wireOp",EDGE,"E25.5"),sQuery(id+"F0.wireOp",EDGE,"E25.6"),sQuery(id+"F0.wireOp",EDGE,"E25.7")])],"isStart":false});
            extrude(context, id + "F17", {"entities" : qUnion([Q0, Q1, Q2]), "endBound" : BoundingType.UP_TO_SURFACE, "endBoundEntityFace" : qUnion([Q3]), "depth" : 25 * mm});
        }
    });
